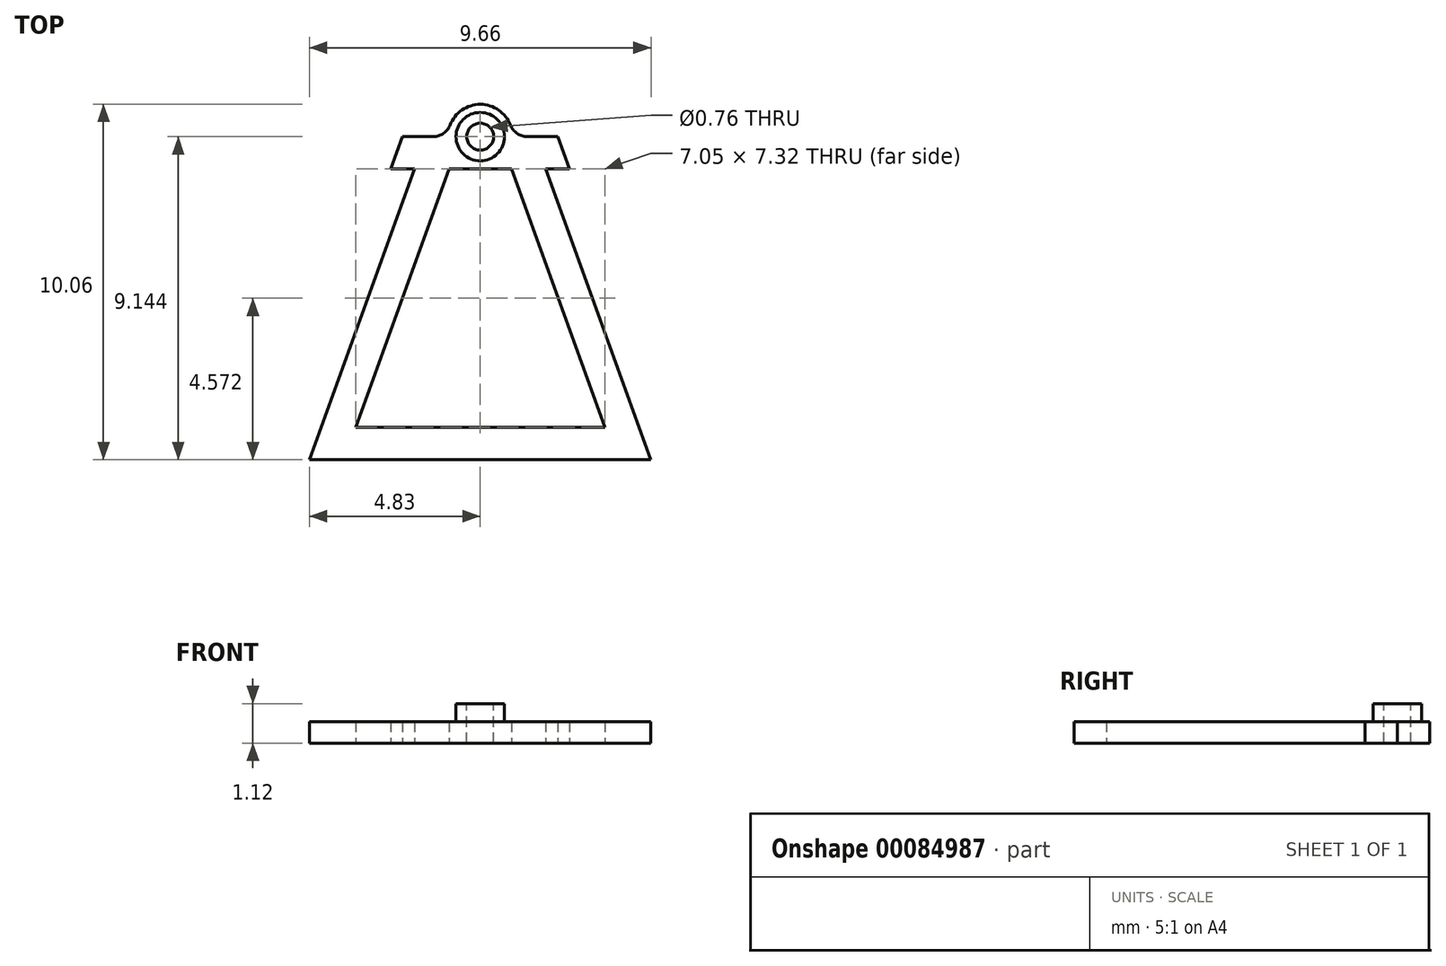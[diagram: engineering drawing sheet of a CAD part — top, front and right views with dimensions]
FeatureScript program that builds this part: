
annotation { "Feature Type Name" : "Feature", "Feature Type Description" : "" }
export const myFeature = defineFeature(function(context is Context, id is Id, definition is map)
    precondition{}
    {
        {
            var Q0;
            Q0=qCreatedBy(makeId("Top.planeOp"),FACE);
            var sketch = newSketch(context, id + "F0", { "sketchPlane" : qUnion([Q0])});
            skLineSegment(sketch, "E0", {"start": v(-4.83, 0) * mm, "end": v(-1.85, 8.23) * mm});
            skLineSegment(sketch, "E1", {"start": v(-1.52, 9.14) * mm, "end": v(-0.91, 9.14) * mm});
            skLineSegment(sketch, "E2", {"start": v(-4.83, 0) * mm, "end": v(0, 0) * mm});
            skLineSegment(sketch, "E3", {"start": v(0, 0) * mm, "end": v(0, 0.91) * mm});
            skLineSegment(sketch, "E4", {"start": v(0, 0.91) * mm, "end": v(-3.52, 0.91) * mm});
            skLineSegment(sketch, "E5", {"start": v(-3.52, 0.91) * mm, "end": v(-0.88, 8.23) * mm});
            skLineSegment(sketch, "E6", {"start": v(-0.88, 8.23) * mm, "end": v(0, 8.23) * mm});
            skLineSegment(sketch, "E7.MirrorCS", {"start": v(4.83, 0) * mm, "end": v(1.85, 8.23) * mm});
            skLineSegment(sketch, "E8.MirrorCS", {"start": v(3.52, 0.91) * mm, "end": v(0.88, 8.23) * mm});
            skLineSegment(sketch, "E9.MirrorCS", {"start": v(1.52, 9.14) * mm, "end": v(0.91, 9.14) * mm});
            skLineSegment(sketch, "E10.MirrorCS", {"start": v(0.88, 8.23) * mm, "end": v(0, 8.23) * mm});
            skLineSegment(sketch, "E11.MirrorCS", {"start": v(0, 0.91) * mm, "end": v(3.52, 0.91) * mm});
            skLineSegment(sketch, "E12.MirrorCS", {"start": v(4.83, 0) * mm, "end": v(0, 0) * mm});
            skLineSegment(sketch, "E13", {"start": v(-1.85, 8.23) * mm, "end": v(-2.53, 8.23) * mm});
            skLineSegment(sketch, "E14", {"start": v(-2.53, 8.23) * mm, "end": v(-2.2, 9.14) * mm});
            skLineSegment(sketch, "E15", {"start": v(-2.2, 9.14) * mm, "end": v(-1.52, 9.14) * mm});
            skLineSegment(sketch, "E16.MirrorCS", {"start": v(2.2, 9.14) * mm, "end": v(1.52, 9.14) * mm});
            skLineSegment(sketch, "E17.MirrorCS", {"start": v(2.53, 8.23) * mm, "end": v(2.2, 9.14) * mm});
            skLineSegment(sketch, "E18.MirrorCS", {"start": v(1.85, 8.23) * mm, "end": v(2.53, 8.23) * mm});
            skArc(sketch, "E19", {"start": v(0.91, 9.14) * mm, "mid": v(0, 10.06) * mm, "end": v(-0.91, 9.14) * mm});
            skPoint(sketch, "E20.orphan", {"position": v(1.52, 9.14) * mm});
            skSolve(sketch);
        }
        {
            var Q0;
            Q0 = qSketchRegion(id + "F0", true);
            extrude(context, id + "F1", {"entities" : qUnion([Q0]), "depth" : 0.6 * mm});
        }
        {
            var Q0;
            Q0=makeQuery(id+"F1.opExtrude","CAP_FACE",FACE,{"disambiguationData":[OSD([sQuery(id+"F0.wireOp",EDGE,"E0"),sQuery(id+"F0.wireOp",EDGE,"E1"),sQuery(id+"F0.wireOp",EDGE,"E2"),sQuery(id+"F0.wireOp",EDGE,"E4"),sQuery(id+"F0.wireOp",EDGE,"E5"),sQuery(id+"F0.wireOp",EDGE,"E6"),sQuery(id+"F0.wireOp",EDGE,"E7.MirrorCS"),sQuery(id+"F0.wireOp",EDGE,"E8.MirrorCS"),sQuery(id+"F0.wireOp",EDGE,"E9.MirrorCS"),sQuery(id+"F0.wireOp",EDGE,"E10.MirrorCS"),sQuery(id+"F0.wireOp",EDGE,"E12.MirrorCS"),sQuery(id+"F0.wireOp",EDGE,"E11.MirrorCS"),sQuery(id+"F0.wireOp",EDGE,"E13"),sQuery(id+"F0.wireOp",EDGE,"E14"),sQuery(id+"F0.wireOp",EDGE,"E15"),sQuery(id+"F0.wireOp",EDGE,"E16.MirrorCS"),sQuery(id+"F0.wireOp",EDGE,"E17.MirrorCS"),sQuery(id+"F0.wireOp",EDGE,"E18.MirrorCS"),sQuery(id+"F0.wireOp",EDGE,"E19")])],"isStart":false});
            var sketch = newSketch(context, id + "F2", { "sketchPlane" : qUnion([Q0])});
            skCircle(sketch, "E21", {"center": v(0, 9.14) * mm, "radius": 0.38 * mm});
            skSolve(sketch);
        }
        {
            var Q0;
            Q0 = qSketchRegion(id + "F2", true);
            extrude(context, id + "F3", {"entities" : qUnion([Q0]), "operationType" : NewBodyOperationType.REMOVE, "oppositeDirection" : true, "depth" : 25.4 * mm});
        }
        {
            var Q0;
            Q0=makeQuery(id+"F1.opExtrude","SWEPT_EDGE",EDGE,{"disambiguationData":[OSD([sQuery(id+"F0.wireOp",EDGE,"E9.MirrorCS"),sQuery(id+"F0.wireOp",EDGE,"E19")])]});
            var Q1;
            Q1=makeQuery(id+"F1.opExtrude","SWEPT_EDGE",EDGE,{"disambiguationData":[OSD([sQuery(id+"F0.wireOp",EDGE,"E1"),sQuery(id+"F0.wireOp",EDGE,"E19")])]});
            fillet(context, id + "F4", {"entities" : qUnion([Q0, Q1]), "radius" : 0.5 * mm, "tangentPropagation" : true, "allowEdgeOverflow" : false});
        }
        {
            var Q0;
            Q0=makeQuery(id+"F1.opExtrude","CAP_FACE",FACE,{"disambiguationData":[OSD([sQuery(id+"F0.wireOp",EDGE,"E0"),sQuery(id+"F0.wireOp",EDGE,"E1"),sQuery(id+"F0.wireOp",EDGE,"E2"),sQuery(id+"F0.wireOp",EDGE,"E4"),sQuery(id+"F0.wireOp",EDGE,"E5"),sQuery(id+"F0.wireOp",EDGE,"E6"),sQuery(id+"F0.wireOp",EDGE,"E7.MirrorCS"),sQuery(id+"F0.wireOp",EDGE,"E8.MirrorCS"),sQuery(id+"F0.wireOp",EDGE,"E9.MirrorCS"),sQuery(id+"F0.wireOp",EDGE,"E10.MirrorCS"),sQuery(id+"F0.wireOp",EDGE,"E12.MirrorCS"),sQuery(id+"F0.wireOp",EDGE,"E11.MirrorCS"),sQuery(id+"F0.wireOp",EDGE,"E13"),sQuery(id+"F0.wireOp",EDGE,"E14"),sQuery(id+"F0.wireOp",EDGE,"E15"),sQuery(id+"F0.wireOp",EDGE,"E16.MirrorCS"),sQuery(id+"F0.wireOp",EDGE,"E17.MirrorCS"),sQuery(id+"F0.wireOp",EDGE,"E18.MirrorCS"),sQuery(id+"F0.wireOp",EDGE,"E19")])],"isStart":false});
            var sketch = newSketch(context, id + "F5", { "sketchPlane" : qUnion([Q0])});
            skCircle(sketch, "E22", {"center": v(0, 9.14) * mm, "radius": 0.38 * mm});
            skCircle(sketch, "E23", {"center": v(0, 9.14) * mm, "radius": 0.69 * mm});
            skSolve(sketch);
        }
        {
            var Q0;
            Q0 = qSketchRegion(id + "F5", true);
            extrude(context, id + "F6", {"entities" : qUnion([Q0]), "operationType" : NewBodyOperationType.ADD, "flatOperationType" : FlatOperationType.REMOVE, "offsetDistance" : 25.4 * mm, "depth" : 0.5 * mm, "domain" : OperationDomain.MODEL});
        }
    });
